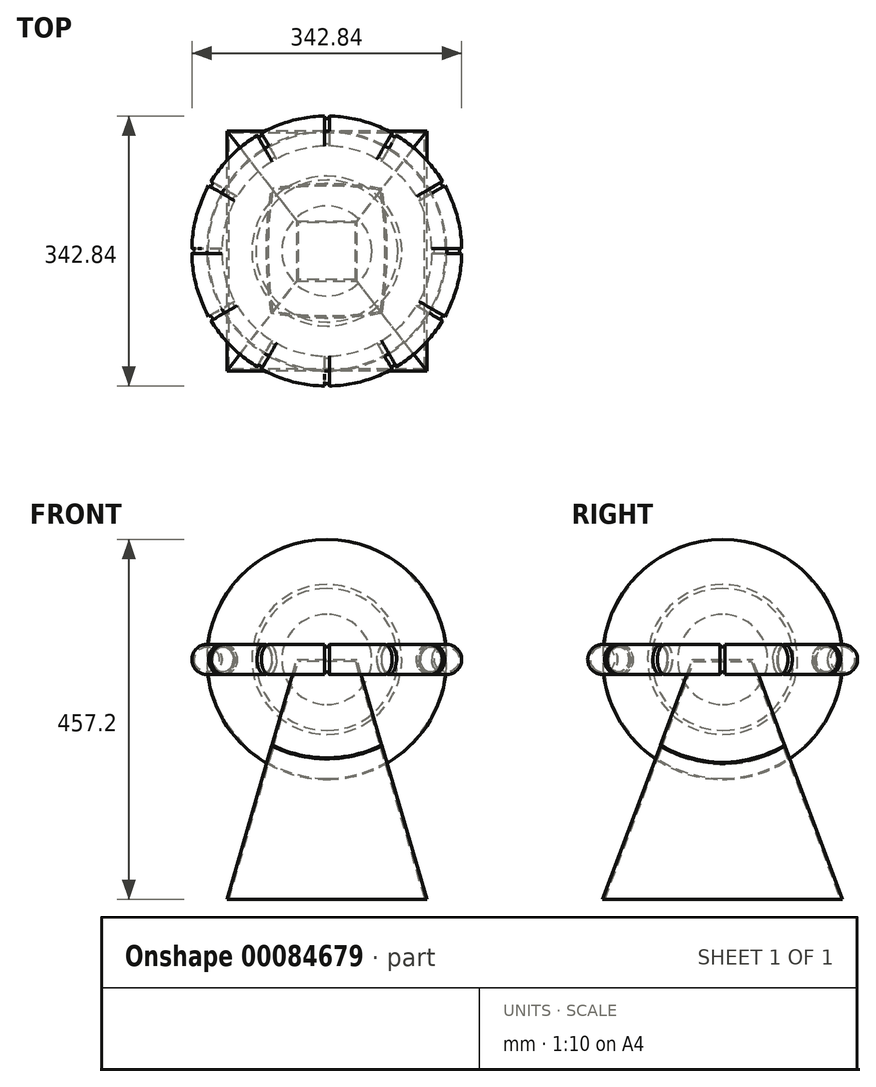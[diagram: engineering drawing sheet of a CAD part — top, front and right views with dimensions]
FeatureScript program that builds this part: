
annotation { "Feature Type Name" : "Feature", "Feature Type Description" : "" }
export const myFeature = defineFeature(function(context is Context, id is Id, definition is map)
    precondition{}
    {
        {
            var Q0;
            Q0=qCreatedBy(makeId("Top.planeOp"),FACE);
            cPlane(context, id + "F0", {"entities" : qUnion([Q0]), "cplaneType" : CPlaneType.OFFSET, "offset" : 152.4 * mm, "oppositeDirection" : true, "width" : 152.4 * mm, "height" : 152.4 * mm});
        }
        {
            var Q0;
            Q0=qCreatedBy(makeId("Top.planeOp"),FACE);
            cPlane(context, id + "F1", {"entities" : qUnion([Q0]), "cplaneType" : CPlaneType.OFFSET, "offset" : 152.4 * mm, "width" : 152.4 * mm, "height" : 152.4 * mm});
        }
        {
            var Q0;
            Q0=qCreatedBy(id+"F0.planeOp",FACE);
            var sketch = newSketch(context, id + "F2", { "sketchPlane" : qUnion([Q0])});
            skLineSegment(sketch, "E0.bottom", {"start": v(127, -152.4) * mm, "end": v(-127, -152.4) * mm});
            skLineSegment(sketch, "E0.top", {"start": v(127, 152.4) * mm, "end": v(-127, 152.4) * mm});
            skLineSegment(sketch, "E0.left", {"start": v(127, -152.4) * mm, "end": v(127, 152.4) * mm});
            skLineSegment(sketch, "E0.right", {"start": v(-127, -152.4) * mm, "end": v(-127, 152.4) * mm});
            skPoint(sketch, "E0.middle", {"position": v(0, 0) * mm});
            skSolve(sketch);
        }
        {
            var Q0;
            Q0=qCreatedBy(id+"F1.planeOp",FACE);
            var sketch = newSketch(context, id + "F3", { "sketchPlane" : qUnion([Q0])});
            skLineSegment(sketch, "E1.bottom", {"start": v(-38.1, -38.1) * mm, "end": v(38.1, -38.1) * mm});
            skLineSegment(sketch, "E1.top", {"start": v(-38.1, 38.1) * mm, "end": v(38.1, 38.1) * mm});
            skLineSegment(sketch, "E1.left", {"start": v(-38.1, -38.1) * mm, "end": v(-38.1, 38.1) * mm});
            skLineSegment(sketch, "E1.right", {"start": v(38.1, -38.1) * mm, "end": v(38.1, 38.1) * mm});
            skPoint(sketch, "E1.middle", {"position": v(0, 0) * mm});
            skSolve(sketch);
        }
        {
            var Q0;
            Q0=makeQuery(id+"F2.imprint","IMPRINT",FACE,{"disambiguationData":[TD([[makeQuery(id+"F2.imprint","IMPRINT",EDGE,{"derivedFrom":sQuery(id+"F2.wireOp",EDGE,"E0.bottom")}),-1.0]])]});
            var Q1;
            Q1=makeQuery(id+"F3.imprint","IMPRINT",FACE,{"disambiguationData":[TD([[makeQuery(id+"F3.imprint","IMPRINT",EDGE,{"derivedFrom":sQuery(id+"F3.wireOp",EDGE,"E1.bottom")}),1.0]])]});
            loft(context, id + "F4", {"sheetProfilesArray" : [{ "sheetProfileEntities" : qUnion([Q0]) }, { "sheetProfileEntities" : qUnion([Q1]) }]});
        }
        {
            var Q0;
            Q0=qCreatedBy(id+"F1.planeOp",FACE);
            var sketch = newSketch(context, id + "F5", { "sketchPlane" : qUnion([Q0])});
            skCircle(sketch, "E2", {"center": v(0, 0) * mm, "radius": 152.4 * mm});
            skSolve(sketch);
        }
        {
            var Q0;
            Q0=qCreatedBy(makeId("Front.planeOp"),FACE);
            var sketch = newSketch(context, id + "F6", { "sketchPlane" : qUnion([Q0])});
            skCircle(sketch, "E3", {"center": v(152.4, 152.4) * mm, "radius": 19.05 * mm});
            skSolve(sketch);
        }
        {
            var Q0;
            Q0=makeQuery(id+"F6.imprint","IMPRINT",FACE,{"disambiguationData":[TD([[makeQuery(id+"F6.imprint","IMPRINT",EDGE,{"derivedFrom":sQuery(id+"F6.wireOp",EDGE,"E3")}),1.0]])]});
            var Q1;
            Q1=sQuery(id+"F5.wireOp",EDGE,"E2");
            revolve(context, id + "F7", {"entities" : qUnion([Q0]), "axis" : qUnion([Q1]), "revolveType" : RevolveType.FULL});
        }
        {
            var Q0;
            Q0=qCreatedBy(makeId("Front.planeOp"),FACE);
            var sketch = newSketch(context, id + "F8", { "sketchPlane" : qUnion([Q0])});
            skArc(sketch, "E4", {"start": v(0, 247.65) * mm, "mid": v(-95.25, 152.4) * mm, "end": v(0, 57.15) * mm});
            skLineSegment(sketch, "E5", {"start": v(0, 57.15) * mm, "end": v(0, 247.65) * mm});
            skSolve(sketch);
        }
        {
            var Q0;
            Q0=makeQuery(id+"F8.imprint","IMPRINT",FACE,{"disambiguationData":[TD([[makeQuery(id+"F8.imprint","IMPRINT",EDGE,{"derivedFrom":sQuery(id+"F8.wireOp",EDGE,"E4")}),1.0]])]});
            var Q1;
            Q1=sQuery(id+"F8.wireOp",EDGE,"E5");
            revolve(context, id + "F9", {"entities" : qUnion([Q0]), "axis" : qUnion([Q1]), "revolveType" : RevolveType.FULL});
        }
        {
            var Q0;
            Q0=makeQuery(id+"F4.opLoft","CAP_FACE",FACE,{"disambiguationData":[OSD([makeQuery(id+"F2.imprint","IMPRINT",FACE,{"disambiguationData":[TD([[makeQuery(id+"F2.imprint","IMPRINT",EDGE,{"derivedFrom":sQuery(id+"F2.wireOp",EDGE,"E0.bottom")}),-1.0]])]})])],"isStart":true});
            shell(context, id + "F10", {"entities" : qUnion([Q0]), "thickness" : 2.54 * mm});
        }
        {
            var Q0;
            Q0=qCreatedBy(id+"F1.planeOp",FACE);
            var sketch = newSketch(context, id + "F11", { "sketchPlane" : qUnion([Q0])});
            skCircle(sketch, "E6", {"center": v(171.45, 0) * mm, "radius": 3.18 * mm});
            skSolve(sketch);
        }
        {
            var Q0;
            Q0=makeQuery(id+"F11.imprint","IMPRINT",FACE,{"disambiguationData":[TD([[makeQuery(id+"F11.imprint","IMPRINT",EDGE,{"derivedFrom":sQuery(id+"F11.wireOp",EDGE,"E6")}),1.0]])]});
            var Q1;
            Q1=sQuery(id+"F6.wireOp",EDGE,"E3");
            revolve(context, id + "F12", {"entities" : qUnion([Q0]), "axis" : qUnion([Q1]), "revolveType" : RevolveType.FULL});
        }
        {
            var Q0;
            Q0=makeQuery(id+"F12.opRevolve","SWEPT_BODY",BODY,{"disambiguationData":[OSD([sQuery(id+"F11.wireOp",EDGE,"E6")])]});
            var Q1;
            Q1=sQuery(id+"F5.wireOp",EDGE,"E2");
            circularPattern(context, id + "F13", {"entities" : qUnion([Q0]), "axis" : qUnion([Q1]), "angle" : 360 * degree, "instanceCount" : 12, "equalSpace" : true});
        }
        {
            var Q0;
            Q0=makeQuery(id+"F12.opRevolve","SWEPT_BODY",BODY,{"disambiguationData":[OSD([sQuery(id+"F11.wireOp",EDGE,"E6")])]});
            var Q1;
            Q1=makeQuery(id+"F13.opPattern","COPY",BODY,{"derivedFrom":makeQuery(id+"F12.opRevolve","SWEPT_BODY",BODY,{"disambiguationData":[OSD([sQuery(id+"F11.wireOp",EDGE,"E6")])]}),"instanceName":"1"});
            var Q2;
            Q2=makeQuery(id+"F13.opPattern","COPY",BODY,{"derivedFrom":makeQuery(id+"F12.opRevolve","SWEPT_BODY",BODY,{"disambiguationData":[OSD([sQuery(id+"F11.wireOp",EDGE,"E6")])]}),"instanceName":"2"});
            var Q3;
            Q3=makeQuery(id+"F13.opPattern","COPY",BODY,{"derivedFrom":makeQuery(id+"F12.opRevolve","SWEPT_BODY",BODY,{"disambiguationData":[OSD([sQuery(id+"F11.wireOp",EDGE,"E6")])]}),"instanceName":"3"});
            var Q4;
            Q4=makeQuery(id+"F13.opPattern","COPY",BODY,{"derivedFrom":makeQuery(id+"F12.opRevolve","SWEPT_BODY",BODY,{"disambiguationData":[OSD([sQuery(id+"F11.wireOp",EDGE,"E6")])]}),"instanceName":"4"});
            var Q5;
            Q5=makeQuery(id+"F13.opPattern","COPY",BODY,{"derivedFrom":makeQuery(id+"F12.opRevolve","SWEPT_BODY",BODY,{"disambiguationData":[OSD([sQuery(id+"F11.wireOp",EDGE,"E6")])]}),"instanceName":"5"});
            var Q6;
            Q6=makeQuery(id+"F13.opPattern","COPY",BODY,{"derivedFrom":makeQuery(id+"F12.opRevolve","SWEPT_BODY",BODY,{"disambiguationData":[OSD([sQuery(id+"F11.wireOp",EDGE,"E6")])]}),"instanceName":"6"});
            var Q7;
            Q7=makeQuery(id+"F13.opPattern","COPY",BODY,{"derivedFrom":makeQuery(id+"F12.opRevolve","SWEPT_BODY",BODY,{"disambiguationData":[OSD([sQuery(id+"F11.wireOp",EDGE,"E6")])]}),"instanceName":"7"});
            var Q8;
            Q8=makeQuery(id+"F13.opPattern","COPY",BODY,{"derivedFrom":makeQuery(id+"F12.opRevolve","SWEPT_BODY",BODY,{"disambiguationData":[OSD([sQuery(id+"F11.wireOp",EDGE,"E6")])]}),"instanceName":"8"});
            var Q9;
            Q9=makeQuery(id+"F13.opPattern","COPY",BODY,{"derivedFrom":makeQuery(id+"F12.opRevolve","SWEPT_BODY",BODY,{"disambiguationData":[OSD([sQuery(id+"F11.wireOp",EDGE,"E6")])]}),"instanceName":"9"});
            var Q10;
            Q10=makeQuery(id+"F13.opPattern","COPY",BODY,{"derivedFrom":makeQuery(id+"F12.opRevolve","SWEPT_BODY",BODY,{"disambiguationData":[OSD([sQuery(id+"F11.wireOp",EDGE,"E6")])]}),"instanceName":"10"});
            var Q11;
            Q11=makeQuery(id+"F13.opPattern","COPY",BODY,{"derivedFrom":makeQuery(id+"F12.opRevolve","SWEPT_BODY",BODY,{"disambiguationData":[OSD([sQuery(id+"F11.wireOp",EDGE,"E6")])]}),"instanceName":"11"});
            var Q12;
            Q12=makeQuery(id+"F7.opRevolve","SWEPT_BODY",BODY,{"disambiguationData":[OSD([sQuery(id+"F6.wireOp",EDGE,"E3")])]});
            booleanBodies(context, id + "F14", {"operationType" : BooleanOperationType.SUBTRACTION, "tools" : qUnion([Q0, Q1, Q2, Q3, Q4, Q5, Q6, Q7, Q8, Q9, Q10, Q11]), "targets" : qUnion([Q12])});
        }
        {
            var Q0;
            Q0=makeQuery(id+"F9.opRevolve","SWEPT_FACE",FACE,{"disambiguationData":[OSD([sQuery(id+"F8.wireOp",EDGE,"E4")])]});
            var Q1;
            Q1=makeQuery(id+"F9.opRevolve","SWEPT_BODY",BODY,{"disambiguationData":[OSD([sQuery(id+"F8.wireOp",EDGE,"E4"),sQuery(id+"F8.wireOp",EDGE,"E5")])]});
            shell(context, id + "F15", {"isHollow" : true, "entities" : qUnion([Q0]), "parts" : qUnion([Q1]), "thickness" : 5.08 * mm});
        }
        {
            var Q0;
            Q0=qCreatedBy(makeId("Front.planeOp"),FACE);
            var sketch = newSketch(context, id + "F16", { "sketchPlane" : qUnion([Q0])});
            skArc(sketch, "E7", {"start": v(0, 209.55) * mm, "mid": v(-57.15, 152.4) * mm, "end": v(0, 95.25) * mm});
            skLineSegment(sketch, "E8", {"start": v(0, 95.25) * mm, "end": v(0, 209.55) * mm});
            skSolve(sketch);
        }
        {
            var Q0;
            Q0 = qSketchRegion(id + "F16", true);
            var Q1;
            Q1=sQuery(id+"F16.wireOp",EDGE,"E7");
            var Q2;
            Q2=sQuery(id+"F8.wireOp",EDGE,"E5");
            revolve(context, id + "F17", {"entities" : qUnion([Q0]), "surfaceEntities" : qUnion([Q1]), "axis" : qUnion([Q2]), "revolveType" : RevolveType.FULL});
        }
        {
            var Q0;
            Q0=qCreatedBy(makeId("Front.planeOp"),FACE);
            var sketch = newSketch(context, id + "F18", { "sketchPlane" : qUnion([Q0])});
            skArc(sketch, "E9", {"start": v(0, 304.8) * mm, "mid": v(-152.4, 152.4) * mm, "end": v(0, 0) * mm});
            skLineSegment(sketch, "E10", {"start": v(0, 304.8) * mm, "end": v(0, 0) * mm});
            skSolve(sketch);
        }
        {
            var Q0;
            Q0=makeQuery(id+"F18.imprint","IMPRINT",FACE,{"disambiguationData":[TD([[makeQuery(id+"F18.imprint","IMPRINT",EDGE,{"derivedFrom":sQuery(id+"F18.wireOp",EDGE,"E9")}),1.0]])]});
            var Q1;
            Q1=sQuery(id+"F18.wireOp",EDGE,"E10");
            revolve(context, id + "F19", {"entities" : qUnion([Q0]), "axis" : qUnion([Q1]), "revolveType" : RevolveType.FULL});
        }
        {
            var Q0;
            Q0=makeQuery(id+"F19.opRevolve","SWEPT_FACE",FACE,{"disambiguationData":[OSD([sQuery(id+"F18.wireOp",EDGE,"E9")])]});
            var Q1;
            Q1=makeQuery(id+"F19.opRevolve","SWEPT_BODY",BODY,{"disambiguationData":[OSD([sQuery(id+"F18.wireOp",EDGE,"E9"),sQuery(id+"F18.wireOp",EDGE,"E10")])]});
            shell(context, id + "F20", {"isHollow" : true, "entities" : qUnion([Q0]), "parts" : qUnion([Q1]), "thickness" : 1.27 * mm});
        }
        {
            var Q0;
            Q0=makeQuery(id+"F19.opRevolve","SWEPT_BODY",BODY,{"disambiguationData":[OSD([sQuery(id+"F18.wireOp",EDGE,"E9"),sQuery(id+"F18.wireOp",EDGE,"E10")])]});
            var Q1;
            Q1=makeQuery(id+"F4.opLoft","SWEPT_BODY",BODY,{"disambiguationData":[OSD([makeQuery(id+"F2.imprint","IMPRINT",FACE,{"disambiguationData":[TD([[makeQuery(id+"F2.imprint","IMPRINT",EDGE,{"derivedFrom":sQuery(id+"F2.wireOp",EDGE,"E0.bottom")}),-1.0]])]}),makeQuery(id+"F3.imprint","IMPRINT",FACE,{"disambiguationData":[TD([[makeQuery(id+"F3.imprint","IMPRINT",EDGE,{"derivedFrom":sQuery(id+"F3.wireOp",EDGE,"E1.bottom")}),1.0]])]})])]});
            booleanBodies(context, id + "F21", {"operationType" : BooleanOperationType.SUBTRACTION, "tools" : qUnion([Q0]), "targets" : qUnion([Q1]), "keepTools" : true});
        }
    });
